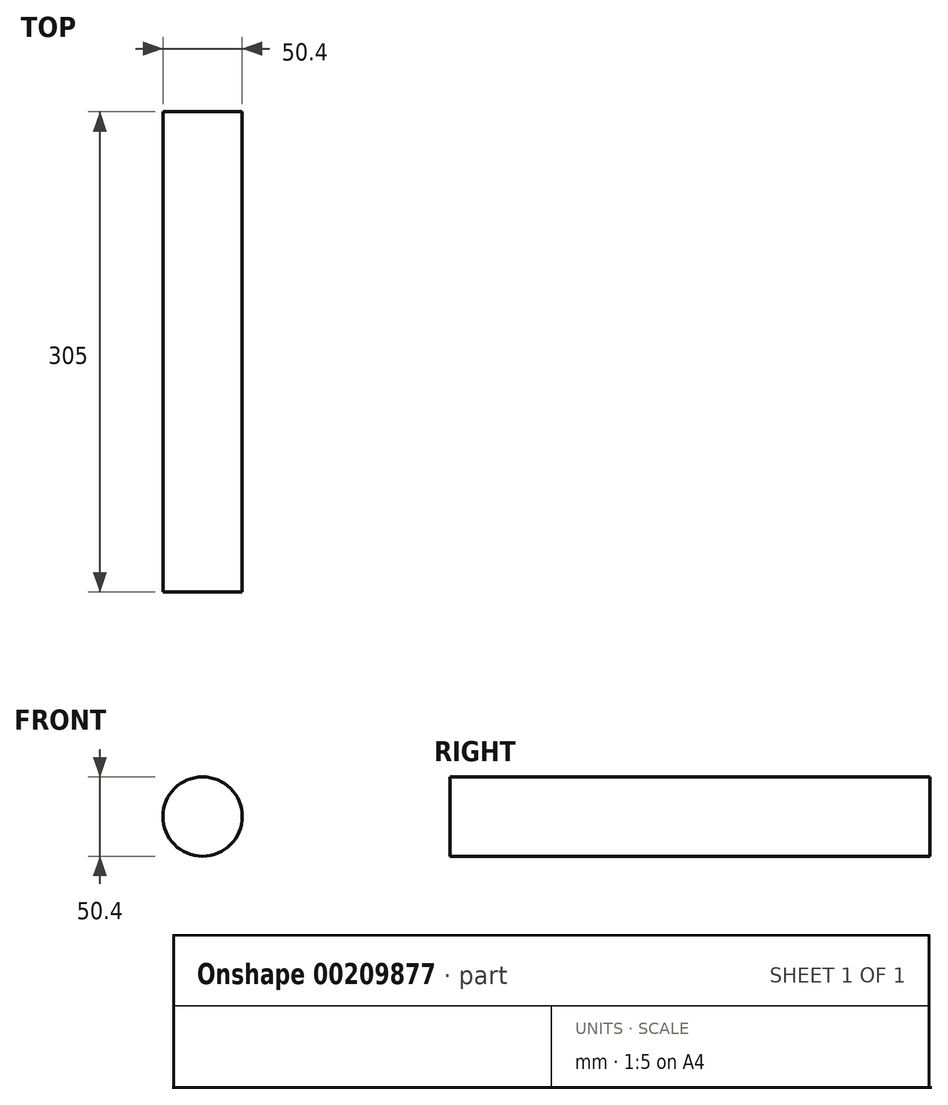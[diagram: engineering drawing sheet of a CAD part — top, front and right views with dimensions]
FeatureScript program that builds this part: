
annotation { "Feature Type Name" : "Feature", "Feature Type Description" : "" }
export const myFeature = defineFeature(function(context is Context, id is Id, definition is map)
    precondition{}
    {
        {
            var Q0;
            Q0=qCreatedBy(makeId("Front.planeOp"),FACE);
            var sketch = newSketch(context, id + "F0", { "sketchPlane" : qUnion([Q0])});
            skCircle(sketch, "E0", {"center": v(0, 0) * mm, "radius": 25.2 * mm});
            skSolve(sketch);
        }
        {
            var Q0;
            Q0=makeQuery(id+"F0.imprint","IMPRINT",FACE,{"disambiguationData":[TD([[makeQuery(id+"F0.imprint","IMPRINT",EDGE,{"derivedFrom":sQuery(id+"F0.wireOp",EDGE,"E0")}),1.0]])]});
            extrude(context, id + "F1", {"entities" : qUnion([Q0]), "depth" : 305 * mm});
        }
    });
